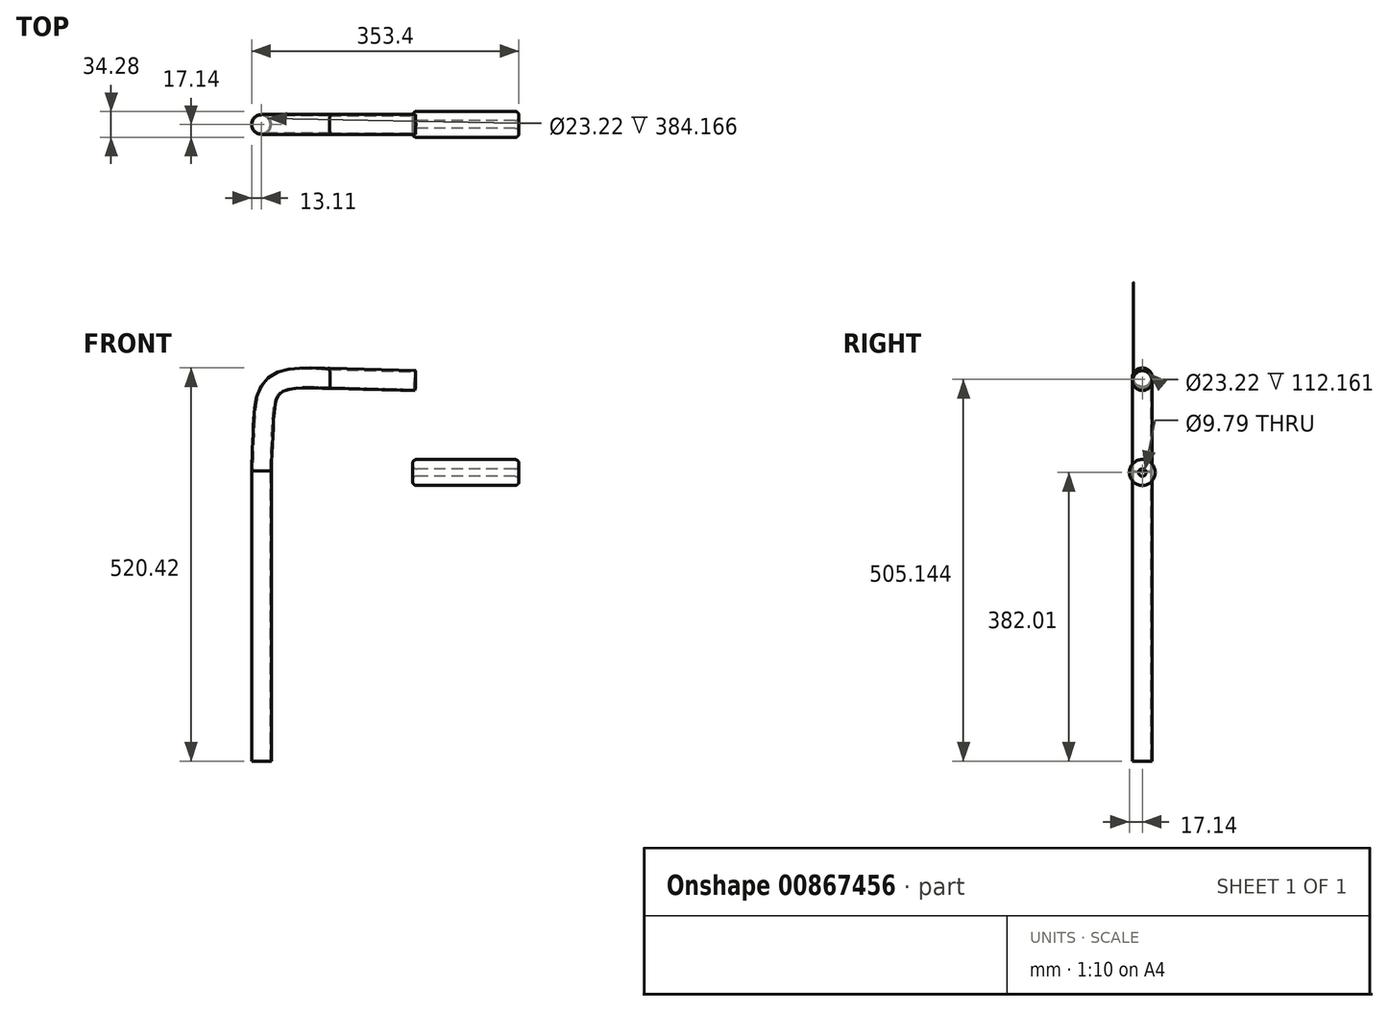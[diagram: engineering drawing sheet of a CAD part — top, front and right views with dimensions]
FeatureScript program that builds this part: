
annotation { "Feature Type Name" : "Feature", "Feature Type Description" : "" }
export const myFeature = defineFeature(function(context is Context, id is Id, definition is map)
    precondition{}
    {
        {
            var Q0;
            Q0=qCreatedBy(makeId("Top.planeOp"),FACE);
            var sketch = newSketch(context, id + "F0", { "sketchPlane" : qUnion([Q0])});
            skCircle(sketch, "E0", {"center": v(0, 0) * mm, "radius": 13.11 * mm});
            skSolve(sketch);
        }
        {
            var Q0;
            Q0=qCreatedBy(makeId("Front.planeOp"),FACE);
            var sketch = newSketch(context, id + "F1", { "sketchPlane" : qUnion([Q0])});
            skLineSegment(sketch, "E1", {"start": v(0, 0) * mm, "end": v(0, 383.97) * mm});
            skLineSegment(sketch, "E2", {"start": v(199.41, 399.15) * mm, "end": v(340.3, 399.15) * mm});
            skLineSegment(sketch, "E3", {"start": v(340.3, 386.9) * mm, "end": v(199.92, 386.9) * mm});
            skLineSegment(sketch, "E4", {"start": v(199.92, 386.9) * mm, "end": v(199.92, 399.15) * mm});
            skLineSegment(sketch, "E5", {"start": v(191.4, 382.01) * mm, "end": v(367.77, 382.01) * mm});
            skLineSegment(sketch, "E6", {"start": v(340.3, 386.9) * mm, "end": v(340.3, 399.15) * mm});
            skFitSpline(sketch, "E7", {"points": [v(0, 383.97) * mm, v(2.89, 452.06) * mm, v(20.35, 499.88) * mm, v(81.02, 506.62) * mm, v(90.46, 506.63) * mm], "startDerivative": vector(7.3, 217.4) * mm, "endDerivative": vector(55.93, 2.82) * mm});
            skLineSegment(sketch, "E8", {"start": v(90.46, 506.63) * mm, "end": v(203.63, 503.6) * mm});
            skSolve(sketch);
        }
        {
            var Q0;
            Q0 = qSketchRegion(id + "F0", true);
            var Q1;
            Q1=sQuery(id+"F1.wireOp",EDGE,"E1");
            var Q2;
            Q2=sQuery(id+"F1.wireOp",EDGE,"06d8ce83-204a-4894-ae80-5685f5204943");
            var Q3;
            Q3=sQuery(id+"F1.wireOp",EDGE,"E7");
            var Q4;
            Q4=sQuery(id+"F1.wireOp",EDGE,"E8");
            sweep(context, id + "F2", {"profiles" : qUnion([Q0]), "path" : qUnion([Q1, Q2, Q3, Q4])});
        }
        {
            var Q0;
            Q0 = qSketchRegion(id + "F0", true);
            extrude(context, id + "F3", {"entities" : qUnion([Q0]), "operationType" : NewBodyOperationType.ADD, "depth" : 25 * mm, "offsetDistance" : 25 * mm});
        }
        {
            var Q0;
            Q0=makeQuery(id+"F1.imprint","IMPRINT",FACE,{"disambiguationData":[TD([[makeQuery(id+"F1.imprint","IMPRINT",EDGE,{"derivedFrom":sQuery(id+"F1.wireOp",EDGE,"E3")}),-1.0]])]});
            var Q1;
            Q1=sQuery(id+"F1.wireOp",EDGE,"E5");
            revolve(context, id + "F4", {"surfaceOperationType" : NewSurfaceOperationType.NEW, "entities" : qUnion([Q0]), "axis" : qUnion([Q1]), "revolveType" : RevolveType.FULL});
        }
        {
            var Q0;
            Q0=makeQuery(id+"F4.opRevolve","SWEPT_FACE",FACE,{"disambiguationData":[OSD([sQuery(id+"F1.wireOp",EDGE,"E6")])]});
            fillet(context, id + "F5", {"entities" : qUnion([Q0]), "radius" : 5 * mm, "tangentPropagation" : true, "allowEdgeOverflow" : false});
        }
        {
            var Q0;
            Q0=makeQuery(id+"F4.opRevolve","SWEPT_FACE",FACE,{"disambiguationData":[OSD([sQuery(id+"F1.wireOp",EDGE,"E4")])]});
            fillet(context, id + "F6", {"entities" : qUnion([Q0]), "radius" : 5 * mm, "tangentPropagation" : true, "allowEdgeOverflow" : false});
        }
        {
            var Q0;
            Q0=makeQuery(id+"F2.opSweep","CAP_FACE",FACE,{"disambiguationData":[OSD([sQuery(id+"F0.wireOp",EDGE,"E0"),sQuery(id+"F1.wireOp",VERTEX,"E1.start")])],"isStart":true});
            shell(context, id + "F7", {"entities" : qUnion([Q0]), "thickness" : 1.5 * mm});
        }
    });
